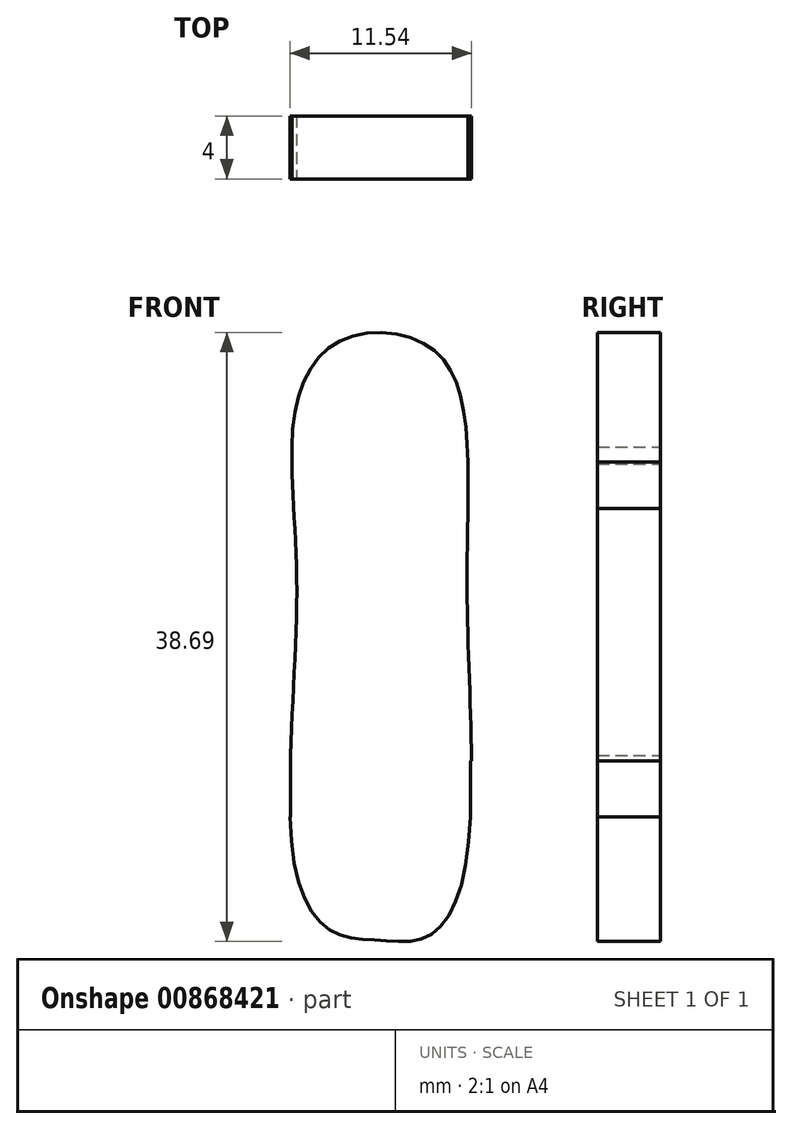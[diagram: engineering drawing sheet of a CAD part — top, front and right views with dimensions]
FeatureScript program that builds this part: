
annotation { "Feature Type Name" : "Feature", "Feature Type Description" : "" }
export const myFeature = defineFeature(function(context is Context, id is Id, definition is map)
    precondition{}
    {
        {
            var Q0;
            Q0=qCreatedBy(makeId("Front.planeOp"),FACE);
            var sketch = newSketch(context, id + "F0", { "sketchPlane" : qUnion([Q0])});
            skFitSpline(sketch, "E0", {"points": [v(-22.11, 6.62) * mm, v(-21.93, 23.98) * mm, v(-21.93, 35.74) * mm, v(-18.75, 39.84) * mm, v(-13.53, 39.28) * mm, v(-11.29, 34.99) * mm, v(-11.1, 23.42) * mm, v(-11.29, 5.88) * mm, v(-13.72, 1.77) * mm, v(-16.7, 1.59) * mm, v(-19.69, 2.15) * mm, v(-22.11, 6.62) * mm]});
            skLineSegment(sketch, "E1.bottom", {"start": v(-22.24, 32.9) * mm, "end": v(-23.8, 32.9) * mm});
            skLineSegment(sketch, "E1.top", {"start": v(-22.24, 29.02) * mm, "end": v(-23.8, 29.02) * mm});
            skLineSegment(sketch, "E1.left", {"start": v(-22.24, 32.9) * mm, "end": v(-22.24, 29.02) * mm});
            skLineSegment(sketch, "E1.right", {"start": v(-23.8, 32.9) * mm, "end": v(-23.8, 29.02) * mm});
            skLineSegment(sketch, "E2.bottom", {"start": v(-22.34, 13.33) * mm, "end": v(-23.8, 13.33) * mm});
            skLineSegment(sketch, "E2.top", {"start": v(-22.34, 9.42) * mm, "end": v(-23.8, 9.42) * mm});
            skLineSegment(sketch, "E2.left", {"start": v(-22.34, 13.33) * mm, "end": v(-22.34, 9.42) * mm});
            skLineSegment(sketch, "E2.right", {"start": v(-23.8, 13.33) * mm, "end": v(-23.8, 9.42) * mm});
            skLineSegment(sketch, "E3.bottom", {"start": v(-10.9, 9.42) * mm, "end": v(-9.42, 9.42) * mm});
            skLineSegment(sketch, "E3.top", {"start": v(-10.9, 12.97) * mm, "end": v(-9.42, 12.97) * mm});
            skLineSegment(sketch, "E3.left", {"start": v(-10.9, 9.42) * mm, "end": v(-10.9, 12.97) * mm});
            skLineSegment(sketch, "E3.right", {"start": v(-9.42, 9.42) * mm, "end": v(-9.42, 12.97) * mm});
            skLineSegment(sketch, "E4.bottom", {"start": v(-11.06, 29.02) * mm, "end": v(-9.42, 29.02) * mm});
            skLineSegment(sketch, "E4.top", {"start": v(-11.06, 32.56) * mm, "end": v(-9.42, 32.56) * mm});
            skLineSegment(sketch, "E4.left", {"start": v(-11.06, 29.02) * mm, "end": v(-11.06, 32.56) * mm});
            skLineSegment(sketch, "E4.right", {"start": v(-9.42, 29.02) * mm, "end": v(-9.42, 32.56) * mm});
            skSolve(sketch);
        }
        {
            var Q0;
            {var subQ8=sQuery(id+"F0.wireOp",EDGE,"E2.left");Q0=makeQuery(id+"F0.imprint","IMPRINT",FACE,{"disambiguationData":[TD([[makeQuery(id+"F0.imprint","IMPRINT",EDGE,{"derivedFrom":subQ8}),1.0]])]});}
            extrude(context, id + "F1", {"entities" : qUnion([Q0]), "depth" : 4 * mm, "offsetDistance" : 25 * mm});
        }
    });
